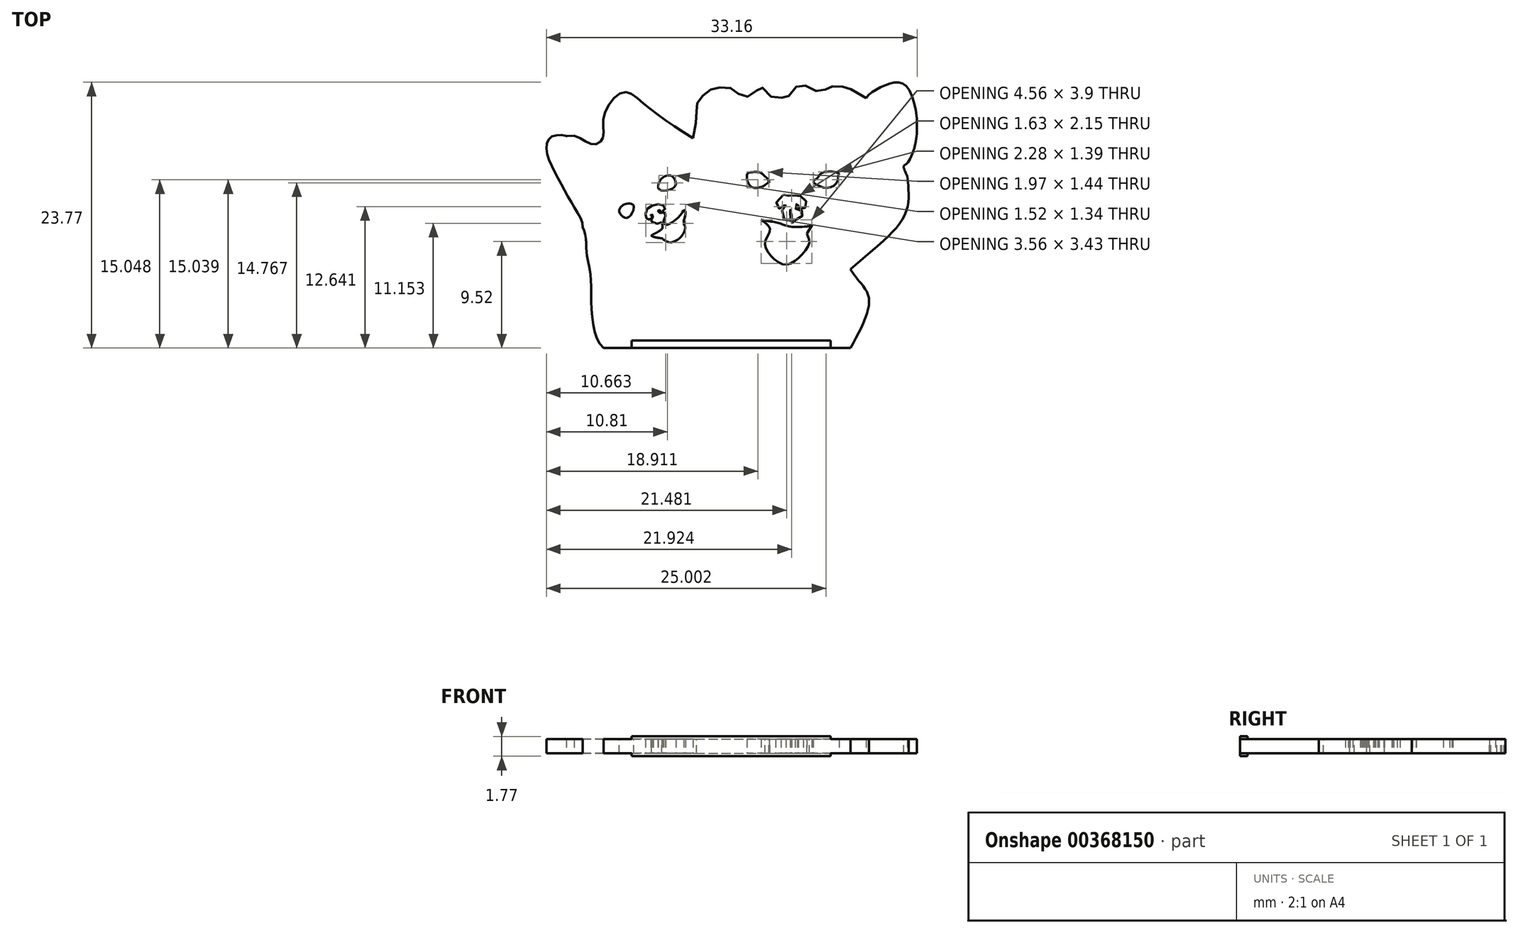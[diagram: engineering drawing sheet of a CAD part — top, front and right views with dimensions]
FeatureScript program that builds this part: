
annotation { "Feature Type Name" : "Feature", "Feature Type Description" : "" }
export const myFeature = defineFeature(function(context is Context, id is Id, definition is map)
    precondition{}
    {
        {
            var Q0;
            Q0=qCreatedBy(makeId("Top.planeOp"),FACE);
            var sketch = newSketch(context, id + "F0", { "sketchPlane" : qUnion([Q0])});
            skFitSpline(sketch, "E0", {"points": [v(-2.44, 3.4) * mm, v(-2.1, 5.5) * mm, v(-2.1, 6.35) * mm, v(-1.7, 7.03) * mm, v(-0.9, 7.71) * mm, v(0, 7.94) * mm, v(1.2, 7.77) * mm, v(1.93, 7.14) * mm, v(3, 7.37) * mm, v(3.63, 8) * mm, v(4.6, 7.09) * mm, v(5.67, 7.03) * mm, v(6.18, 7.2) * mm, v(7.14, 8.22) * mm, v(8.28, 7.71) * mm, v(9.36, 7.71) * mm, v(9.87, 8) * mm, v(10.94, 8) * mm, v(11.68, 7.77) * mm, v(12.2, 7.48) * mm, v(13.06, 6.96) * mm], "startDerivative": vector(6.79, 31.67) * mm, "endDerivative": vector(14.87, -9.58) * mm});
            skFitSpline(sketch, "E1", {"points": [v(-2.44, 3.4) * mm, v(-6.7, 6.35) * mm, v(-8.67, 7.48) * mm, v(-10.44, 5.27) * mm, v(-10.49, 3.4) * mm, v(-11.4, 2.83) * mm, v(-13.06, 3.6) * mm], "startDerivative": vector(-19.8, 12.61) * mm, "endDerivative": vector(-12.53, 2.56) * mm});
            skFitSpline(sketch, "E2", {"points": [v(-12.3, -4.6) * mm, v(-11.96, -6.92) * mm, v(-11.59, -9.01) * mm, v(-10.44, -15.38) * mm], "startDerivative": vector(4.03, -5.46) * mm, "endDerivative": vector(8.77, -7.4) * mm});
            skFitSpline(sketch, "E3", {"points": [v(-2.44, 3.4) * mm, v(-2.95, 0) * mm, v(-0.9, -5.39) * mm, v(1.59, -7.77) * mm, v(1.2, -9.92) * mm, v(2.24, -15.38) * mm], "startDerivative": vector(-4.53, -16.01) * mm, "endDerivative": vector(5.8, -20.44) * mm});
            skFitSpline(sketch, "E4", {"points": [v(2.44, 0.2) * mm, v(2.93, 0.35) * mm, v(3.55, 0.32) * mm, v(4.4, -0.5) * mm, v(4.24, -0.64) * mm, v(3.87, -0.9) * mm, v(3.18, -1.06) * mm, v(2.62, -0.8) * mm, v(2.44, 0.2) * mm]});
            skFitSpline(sketch, "E5", {"points": [v(8.32, -0.49) * mm, v(8.67, -0.2) * mm, v(9, 0.2) * mm, v(9.92, 0.4) * mm, v(10.65, 0.2) * mm, v(10.58, 0.05) * mm, v(10.51, -0.42) * mm, v(9.8, -1.03) * mm, v(8.72, -0.83) * mm, v(8.32, -0.49) * mm]});
            skFitSpline(sketch, "E6", {"points": [v(-5.47, -1.2) * mm, v(-5.38, -0.4) * mm, v(-4.9, 0) * mm, v(-4.32, 0) * mm, v(-3.97, -0.66) * mm, v(-4.32, -1.13) * mm, v(-5.47, -1.2) * mm]});
            skFitSpline(sketch, "E7", {"points": [v(-7.72, -2.7) * mm, v(-8.18, -2.44) * mm, v(-8.79, -2.66) * mm, v(-9.02, -3.17) * mm, v(-8.35, -3.74) * mm, v(-7.72, -2.7) * mm]});
            skFitSpline(sketch, "E8", {"points": [v(-7.75, -3.02) * mm, v(-7.98, -2.7) * mm, v(-8.18, -2.64) * mm, v(-8.51, -2.7) * mm, v(-8.78, -2.91) * mm, v(-8.86, -3.18) * mm, v(-8.63, -3.47) * mm, v(-8.33, -3.54) * mm, v(-8.02, -3.38) * mm, v(-7.79, -3.1) * mm], "startDerivative": vector(-1.75, 3.16) * mm, "endDerivative": vector(1.83, 2.47) * mm});
            skFitSpline(sketch, "E9", {"points": [v(-5.32, -1.12) * mm, v(-5.32, -1) * mm, v(-5.27, -0.5) * mm, v(-4.8, -0.07) * mm, v(-4.32, -0.2) * mm, v(-4.22, -0.72) * mm, v(-4.62, -1.1) * mm, v(-5.32, -1.12) * mm]});
            skFitSpline(sketch, "E10", {"points": [v(2.74, 0.14) * mm, v(3, 0.24) * mm, v(3.4, 0.26) * mm, v(3.8, 0.04) * mm, v(4.02, -0.16) * mm, v(4.06, -0.77) * mm], "startDerivative": vector(1.44, 0.6) * mm, "endDerivative": vector(-0.12, -2.85) * mm});
            skFitSpline(sketch, "E11", {"points": [v(2.74, 0.14) * mm, v(2.62, -0.03) * mm, v(2.54, -0.47) * mm, v(2.93, -1.03) * mm], "startDerivative": vector(-0.48, -0.64) * mm, "endDerivative": vector(1.21, -1.3) * mm});
            skFitSpline(sketch, "E12", {"points": [v(9.26, -0.9) * mm, v(8.92, -0.7) * mm, v(8.85, -0.19) * mm, v(9.15, 0.14) * mm, v(9.79, 0.28) * mm, v(10.28, 0.09) * mm, v(10.28, -0.49) * mm, v(9.9, -0.9) * mm, v(9.26, -0.9) * mm]});
            skFitSpline(sketch, "E13", {"points": [v(-6.62, -3.06) * mm, v(-5.88, -2.56) * mm, v(-5.16, -2.56) * mm, v(-4.93, -2.9) * mm, v(-5.3, -3.25) * mm, v(-5.45, -3.02) * mm, v(-5.54, -3.06) * mm, v(-5.56, -3.15) * mm, v(-5.4, -3.3) * mm, v(-5.02, -3.25) * mm, v(-4.88, -3.44) * mm, v(-5.18, -4.1) * mm, v(-5.54, -3.62) * mm, v(-5.62, -3.67) * mm, v(-5.22, -4.13) * mm, v(-5.82, -4.23) * mm, v(-6.21, -3.94) * mm, v(-6.15, -3.88) * mm, v(-6.03, -3.75) * mm, v(-6, -3.57) * mm, v(-6.11, -3.44) * mm, v(-6.2, -3.45) * mm, v(-6.22, -3.51) * mm, v(-6.11, -3.54) * mm, v(-6.05, -3.63) * mm, v(-6.15, -3.78) * mm, v(-6.34, -3.88) * mm, v(-6.5, -3.87) * mm, v(-6.64, -3.66) * mm, v(-6.62, -3.06) * mm]});
            skFitSpline(sketch, "E14", {"points": [v(5.66, -1.67) * mm, v(6.02, -1.72) * mm, v(6.46, -1.79) * mm, v(6.74, -1.7) * mm, v(7.36, -1.89) * mm, v(7.75, -2.46) * mm, v(7.52, -2.9) * mm, v(7.03, -2.95) * mm, v(6.92, -2.72) * mm, v(7.01, -2.5) * mm, v(6.92, -2.46) * mm, v(6.76, -2.63) * mm, v(6.78, -2.94) * mm, v(7.3, -3.1) * mm, v(7.45, -3.28) * mm, v(7.1, -3.83) * mm, v(6.7, -3.9) * mm, v(6.38, -4.2) * mm, v(6.36, -2.98) * mm, v(6.28, -2.99) * mm, v(6.23, -4.16) * mm, v(5.44, -3.2) * mm, v(5.87, -2.84) * mm, v(5.76, -2.47) * mm, v(5.68, -2.62) * mm, v(5.47, -2.92) * mm, v(4.98, -2.63) * mm, v(5.66, -1.67) * mm]});
            skFitSpline(sketch, "E15", {"points": [v(-6.11, -5.27) * mm, v(-5.18, -4.66) * mm, v(-5.18, -4.35) * mm, v(-5.22, -4.14) * mm], "startDerivative": vector(2.46, 1.2) * mm, "endDerivative": vector(-0.14, 0.9) * mm});
            skFitSpline(sketch, "E16", {"points": [v(-6.11, -5.27) * mm, v(-6.11, -5.37) * mm, v(-5.38, -5.55) * mm, v(-5.22, -5.53) * mm, v(-5.5, -5.33) * mm, v(-5.47, -5.2) * mm, v(-4.97, -5.27) * mm, v(-4.96, -5.4) * mm, v(-4.84, -5.37) * mm, v(-4.71, -5.37) * mm, v(-4.54, -5.27) * mm, v(-4.46, -5.27) * mm, v(-4.38, -5.16) * mm, v(-4.29, -5.14) * mm, v(-4.17, -5.07) * mm, v(-4.03, -5.07) * mm, v(-4.04, -4.98) * mm, v(-3.9, -4.86) * mm, v(-3.81, -4.66) * mm, v(-3.93, -4.61) * mm, v(-3.9, -4.46) * mm, v(-3.9, -4.13) * mm, v(-3.8, -3.93) * mm, v(-3.62, -4.1) * mm, v(-3.56, -4.66) * mm, v(-3.64, -4.66) * mm, v(-3.6, -4.78) * mm, v(-3.67, -4.9) * mm, v(-3.76, -4.91) * mm, v(-3.78, -5.07) * mm, v(-3.87, -5.2) * mm, v(-3.98, -5.2) * mm, v(-4.06, -5.27) * mm, v(-4.14, -5.34) * mm, v(-4.21, -5.43) * mm, v(-4.37, -5.45) * mm, v(-4.4, -5.55) * mm, v(-4.64, -5.62) * mm, v(-4.76, -5.69) * mm, v(-4.98, -5.62) * mm, v(-5.06, -5.68) * mm, v(-5.18, -5.56) * mm], "startDerivative": vector(-2.37, -5.4) * mm, "endDerivative": vector(-5.48, 8.16) * mm});
            skFitSpline(sketch, "E17", {"points": [v(-5.18, -5.56) * mm, v(-5.22, -5.53) * mm], "startDerivative": vector(-0.04, 0.02) * mm, "endDerivative": vector(-0.04, 0.02) * mm});
            skFitSpline(sketch, "E18", {"points": [v(-5.08, -4.04) * mm, v(-4.83, -4.35) * mm, v(-3.52, -3.44) * mm, v(-3.22, -3.04) * mm, v(-3.1, -3.25) * mm, v(-3.27, -4.27) * mm, v(-3.12, -4.53) * mm, v(-3.38, -5.27) * mm, v(-3.87, -5.73) * mm, v(-4.46, -5.94) * mm, v(-5.13, -5.63) * mm], "startDerivative": vector(1.9, -5.74) * mm, "endDerivative": vector(-6.26, 4.24) * mm});
            skFitSpline(sketch, "E19", {"points": [v(-5.45, -5.07) * mm, v(-5.53, -4.97) * mm], "startDerivative": vector(-0.08, 0.1) * mm, "endDerivative": vector(-0.08, 0.1) * mm});
            skFitSpline(sketch, "E20", {"points": [v(-5.48, -5.04) * mm, v(-5.4, -5.18) * mm], "startDerivative": vector(0.09, -0.14) * mm, "endDerivative": vector(0.09, -0.14) * mm});
            skFitSpline(sketch, "E21", {"points": [v(-4.97, -5.27) * mm, v(-4.84, -5.37) * mm, v(-4.54, -5.27) * mm, v(-3.81, -4.66) * mm], "startDerivative": vector(0.55, -0.64) * mm, "endDerivative": vector(1.57, 1.42) * mm});
            skFitSpline(sketch, "E22", {"points": [v(-3.8, -3.93) * mm, v(-3.8, -3.81) * mm, v(-3.81, -3.75) * mm], "startDerivative": vector(0, 0.21) * mm, "endDerivative": vector(-0.02, 0.15) * mm});
            skFitSpline(sketch, "E23", {"points": [v(2.2, -2.92) * mm, v(3.2, -3.77) * mm, v(5.13, -4.18) * mm, v(6.23, -4.5) * mm, v(9.06, -4.2) * mm, v(10.43, -3.14) * mm], "startDerivative": vector(4.72, -5.7) * mm, "endDerivative": vector(5.48, 6.1) * mm});
            skFitSpline(sketch, "E24", {"points": [v(3.66, -3.91) * mm, v(4.35, -4.5) * mm, v(4.43, -5) * mm, v(4.02, -5.84) * mm, v(4.4, -6.95) * mm, v(5.76, -7.92) * mm, v(7.17, -7.18) * mm, v(7.99, -5.88) * mm, v(7.76, -5.14) * mm, v(7.75, -4.5) * mm], "startDerivative": vector(7.9, -5.75) * mm, "endDerivative": vector(0.8, 7.3) * mm});
            skFitSpline(sketch, "E25", {"points": [v(7.76, -5.14) * mm, v(8.22, -4.44) * mm], "startDerivative": vector(0.46, 0.7) * mm, "endDerivative": vector(0.46, 0.7) * mm});
            skFitSpline(sketch, "E26", {"points": [v(4.35, -4.5) * mm, v(4.35, -4.18) * mm], "startDerivative": vector(0, 0.33) * mm, "endDerivative": vector(0, 0.33) * mm});
            skFitSpline(sketch, "E27", {"points": [v(4.35, -4.18) * mm, v(4.35, -4.04) * mm], "startDerivative": vector(0, 0.14) * mm, "endDerivative": vector(0, 0.14) * mm});
            skFitSpline(sketch, "E28", {"points": [v(-13.06, 3.6) * mm, v(-13.78, 3.6) * mm, v(-14.94, 3.6) * mm, v(-15.54, 2.5) * mm, v(-14.62, 0) * mm, v(-13.06, -2.78) * mm, v(-12.3, -4.6) * mm], "startDerivative": vector(-25.45, 0) * mm, "endDerivative": vector(-0.55, -9.34) * mm});
            skFitSpline(sketch, "E29", {"points": [v(13.06, 6.96) * mm, v(14.8, 8.14) * mm, v(16.56, 8.14) * mm, v(17.58, 3.6) * mm, v(16.62, 1.04) * mm, v(16.74, 0) * mm, v(16.93, -5.1) * mm], "startDerivative": vector(7.1, 10.61) * mm, "endDerivative": vector(-67.75, 63.2) * mm});
            skFitSpline(sketch, "E30", {"points": [v(16.62, 1.04) * mm, v(16.74, 0) * mm, v(16.62, -3.24) * mm, v(11.66, -8.33) * mm], "startDerivative": vector(2.45, -6.35) * mm, "endDerivative": vector(-12.46, -11.06) * mm});
            skFitSpline(sketch, "E31", {"points": [v(11.66, -8.33) * mm, v(12.4, -9.34) * mm, v(13.32, -11) * mm, v(11.66, -15.38) * mm], "startDerivative": vector(2.75, -4.07) * mm, "endDerivative": vector(-5.77, -10.48) * mm});
            skLineSegment(sketch, "E32", {"start": v(-10.44, -15.38) * mm, "end": v(2.24, -15.38) * mm});
            skLineSegment(sketch, "E33", {"start": v(2.24, -15.38) * mm, "end": v(11.66, -15.38) * mm});
            skLineSegment(sketch, "E34.bottom", {"start": v(-7.93, -14.7) * mm, "end": v(9.9, -14.7) * mm});
            skLineSegment(sketch, "E34.top", {"start": v(-7.93, -15.38) * mm, "end": v(9.9, -15.38) * mm});
            skLineSegment(sketch, "E34.left", {"start": v(-7.93, -14.7) * mm, "end": v(-7.93, -15.38) * mm});
            skLineSegment(sketch, "E34.right", {"start": v(9.9, -14.7) * mm, "end": v(9.9, -15.38) * mm});
            skPoint(sketch, "E35", {"position": v(2.04, -14.7) * mm});
            skSolve(sketch);
        }
        {
            var Q0;
            Q0=makeQuery(id+"F0.imprint","IMPRINT",FACE,{"disambiguationData":[TD([[makeQuery(id+"F0.imprint","IMPRINT",EDGE,{"derivedFrom":sQuery(id+"F0.wireOp",EDGE,"E0")}),-1.0]])]});
            extrude(context, id + "F1", {"entities" : qUnion([Q0]), "depth" : 1.27 * mm});
        }
        {
            var Q0;
            Q0=makeQuery(id+"F0.imprint","IMPRINT",FACE,{"disambiguationData":[TD([[makeQuery(id+"F0.imprint","IMPRINT",EDGE,{"derivedFrom":sQuery(id+"F0.wireOp",EDGE,"E1")}),1.0]])]});
            extrude(context, id + "F2", {"entities" : qUnion([Q0]), "operationType" : NewBodyOperationType.ADD, "depth" : 1.27 * mm});
        }
        {
            var Q0;
            Q0=sQuery(id+"F0.wireOp",EDGE,"E3");
            extrude(context, id + "F3", {"bodyType" : ToolBodyType.SURFACE, "surfaceEntities" : qUnion([Q0]), "depth" : 1.52 * mm});
        }
        {
            var Q0;
            {var subQ3=sQuery(id+"F0.wireOp",EDGE,"E34.bottom");var subQ5=sQuery(id+"F0.wireOp",EDGE,"E34.left");var subQ7=makeQuery(id+"F0.imprint","INTERSECT",VERTEX,{"derivedFrom":[subQ3,subQ5]});Q0=makeQuery(id+"F0.imprint","IMPRINT",FACE,{"disambiguationData":[TD([[makeQuery(id+"F0.imprint","IMPRINT",EDGE,{"disambiguationData":[TD([[subQ7,-1.0]])],"derivedFrom":subQ3}),-1.0]])]});}
            var Q1;
            {var subQ5=sQuery(id+"F0.wireOp",EDGE,"E34.right");Q1=makeQuery(id+"F0.imprint","IMPRINT",FACE,{"disambiguationData":[TD([[makeQuery(id+"F0.imprint","IMPRINT",EDGE,{"derivedFrom":subQ5}),-1.0]])]});}
            extrude(context, id + "F4", {"entities" : qUnion([Q0, Q1]), "operationType" : NewBodyOperationType.ADD, "depth" : 1.52 * mm});
        }
        {
            var Q0;
            {var subQ5=sQuery(id+"F0.wireOp",EDGE,"E34.right");Q0=makeQuery(id+"F0.imprint","IMPRINT",FACE,{"disambiguationData":[TD([[makeQuery(id+"F0.imprint","IMPRINT",EDGE,{"derivedFrom":subQ5}),-1.0]])]});}
            var Q1;
            {var subQ3=sQuery(id+"F0.wireOp",EDGE,"E34.bottom");var subQ5=sQuery(id+"F0.wireOp",EDGE,"E34.left");var subQ7=makeQuery(id+"F0.imprint","INTERSECT",VERTEX,{"derivedFrom":[subQ3,subQ5]});Q1=makeQuery(id+"F0.imprint","IMPRINT",FACE,{"disambiguationData":[TD([[makeQuery(id+"F0.imprint","IMPRINT",EDGE,{"disambiguationData":[TD([[subQ7,-1.0]])],"derivedFrom":subQ3}),-1.0]])]});}
            extrude(context, id + "F5", {"entities" : qUnion([Q0, Q1]), "operationType" : NewBodyOperationType.ADD, "oppositeDirection" : true, "depth" : 0.25 * mm});
        }
    });
